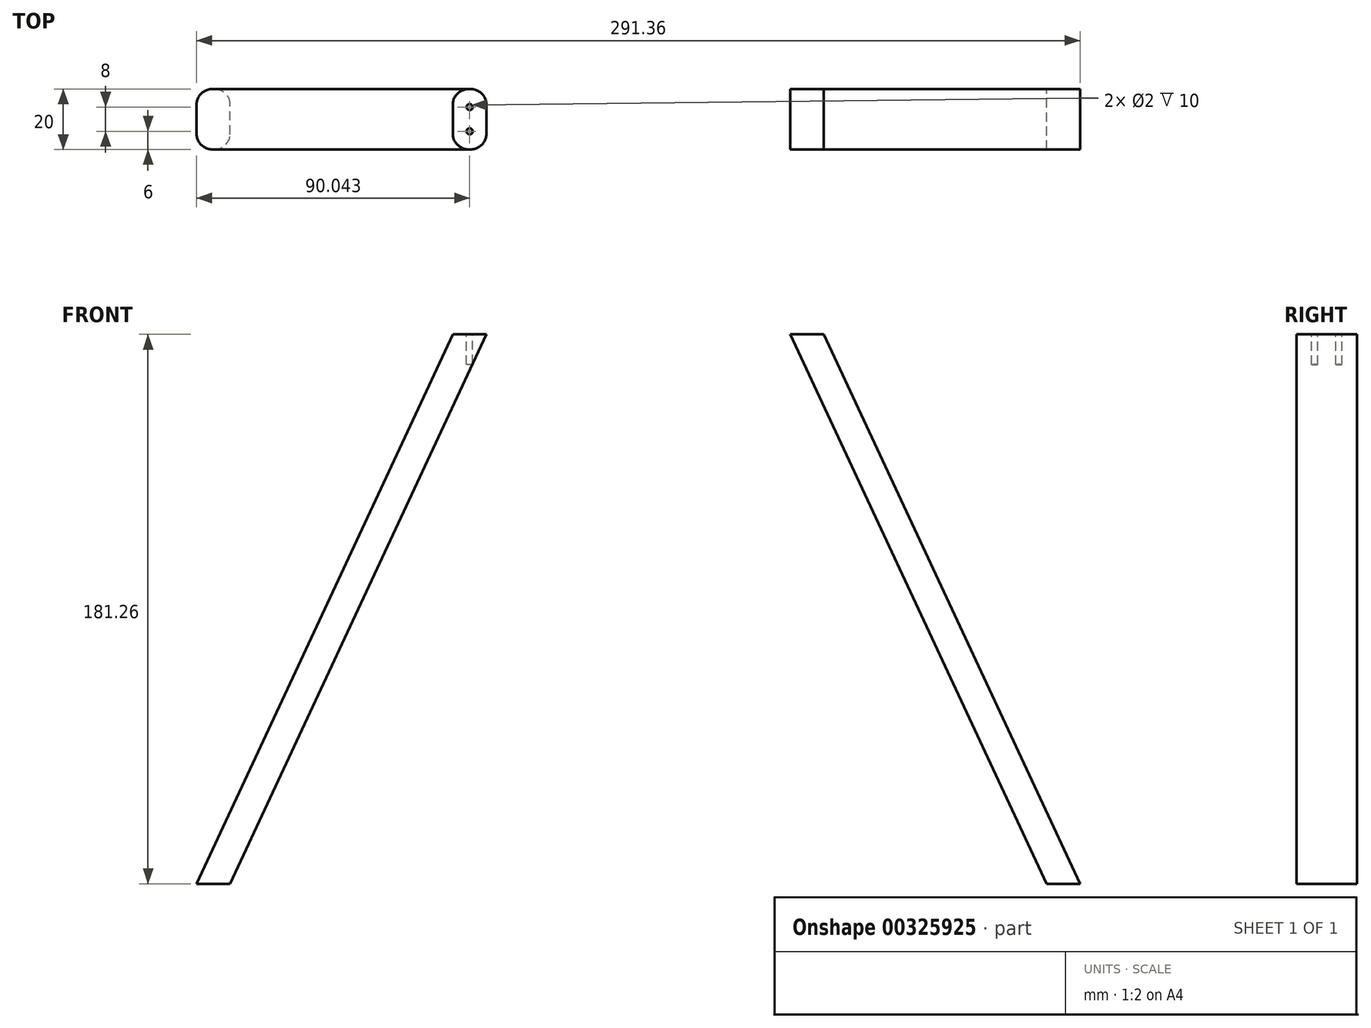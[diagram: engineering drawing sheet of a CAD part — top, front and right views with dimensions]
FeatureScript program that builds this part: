
annotation { "Feature Type Name" : "Feature", "Feature Type Description" : "" }
export const myFeature = defineFeature(function(context is Context, id is Id, definition is map)
    precondition{}
    {
        {
            var Q0;
            Q0=qCreatedBy(makeId("Front.planeOp"),FACE);
            var sketch = newSketch(context, id + "F0", { "sketchPlane" : qUnion([Q0])});
            skLineSegment(sketch, "E0", {"start": v(501.5, 0) * mm, "end": v(586.02, 181.26) * mm});
            skLineSegment(sketch, "E1", {"start": v(501.5, 0) * mm, "end": v(512.53, 0) * mm});
            skLineSegment(sketch, "E2", {"start": v(512.53, 0) * mm, "end": v(597.05, 181.26) * mm});
            skLineSegment(sketch, "E3", {"start": v(597.05, 181.26) * mm, "end": v(586.02, 181.26) * mm});
            skLineSegment(sketch, "E4", {"start": v(647.17, 222.71) * mm, "end": v(647.17, 393.03) * mm, "construction": true});
            skLineSegment(sketch, "E5.MirrorCS", {"start": v(792.85, 0) * mm, "end": v(781.82, 0) * mm});
            skLineSegment(sketch, "E6.MirrorCS", {"start": v(697.3, 181.26) * mm, "end": v(708.33, 181.26) * mm});
            skLineSegment(sketch, "E7.MirrorCS", {"start": v(792.85, 0) * mm, "end": v(708.33, 181.26) * mm});
            skLineSegment(sketch, "E8.MirrorCS", {"start": v(781.82, 0) * mm, "end": v(697.3, 181.26) * mm});
            skSolve(sketch);
        }
        {
            var Q0;
            Q0=makeQuery(id+"F0.imprint","IMPRINT",FACE,{"disambiguationData":[TD([[makeQuery(id+"F0.imprint","IMPRINT",EDGE,{"derivedFrom":sQuery(id+"F0.wireOp",EDGE,"E0")}),-1.0]])]});
            var Q1;
            Q1=makeQuery(id+"F0.imprint","IMPRINT",FACE,{"disambiguationData":[TD([[makeQuery(id+"F0.imprint","IMPRINT",EDGE,{"derivedFrom":sQuery(id+"F0.wireOp",EDGE,"E5.MirrorCS")}),-1.0]])]});
            extrude(context, id + "F1", {"entities" : qUnion([Q0, Q1]), "depth" : 20 * mm});
        }
        {
            var Q0;
            Q0=makeQuery(id+"F1.opExtrude","SWEPT_FACE",FACE,{"disambiguationData":[OSD([sQuery(id+"F0.wireOp",EDGE,"E3")])]});
            var sketch = newSketch(context, id + "F2", { "sketchPlane" : qUnion([Q0])});
            skCircle(sketch, "E9", {"center": v(591.53, -6) * mm, "radius": 1 * mm});
            skPoint(sketch, "E9.centerSnap0", {"position": v(591.53, 0) * mm});
            skCircle(sketch, "E10", {"center": v(591.53, -14) * mm, "radius": 1 * mm});
            skSolve(sketch);
        }
        {
            var Q0;
            Q0=makeQuery(id+"F2.imprint","IMPRINT",FACE,{"disambiguationData":[TD([[makeQuery(id+"F2.imprint","IMPRINT",EDGE,{"derivedFrom":sQuery(id+"F2.wireOp",EDGE,"E9")}),1.0]])]});
            var Q1;
            Q1=makeQuery(id+"F2.imprint","IMPRINT",FACE,{"disambiguationData":[TD([[makeQuery(id+"F2.imprint","IMPRINT",EDGE,{"derivedFrom":sQuery(id+"F2.wireOp",EDGE,"E10")}),1.0]])]});
            var Q2;
            Q2=sQuery(id+"F2.wireOp",EDGE,"E10");
            var Q3;
            Q3=sQuery(id+"F2.wireOp",EDGE,"E9");
            extrude(context, id + "F3", {"entities" : qUnion([Q0, Q1]), "operationType" : NewBodyOperationType.REMOVE, "surfaceEntities" : qUnion([Q2, Q3]), "oppositeDirection" : true, "depth" : 10 * mm});
        }
        {
            var Q0;
            Q0=makeQuery(id+"F1.opExtrude","CAP_EDGE",EDGE,{"disambiguationData":[OSD([sQuery(id+"F0.wireOp",EDGE,"E0")])],"isStart":false});
            var Q1;
            Q1=makeQuery(id+"F1.opExtrude","CAP_EDGE",EDGE,{"disambiguationData":[OSD([sQuery(id+"F0.wireOp",EDGE,"E0")])],"isStart":true});
            var Q2;
            Q2=makeQuery(id+"F1.opExtrude","CAP_EDGE",EDGE,{"disambiguationData":[OSD([sQuery(id+"F0.wireOp",EDGE,"E2")])],"isStart":false});
            var Q3;
            Q3=makeQuery(id+"F1.opExtrude","CAP_EDGE",EDGE,{"disambiguationData":[OSD([sQuery(id+"F0.wireOp",EDGE,"E2")])],"isStart":true});
            fillet(context, id + "F4", {"entities" : qUnion([Q0, Q1, Q2, Q3]), "radius" : 5 * mm, "tangentPropagation" : true, "allowEdgeOverflow" : false});
        }
    });
